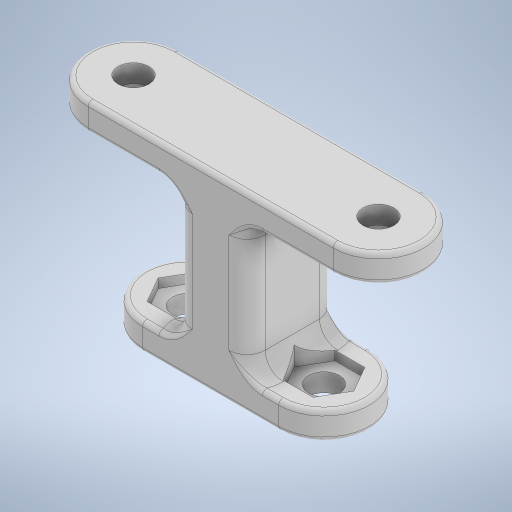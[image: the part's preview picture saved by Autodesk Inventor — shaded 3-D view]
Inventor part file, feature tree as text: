
AUTODESK INVENTOR PART (.ipt)
format: ipt  version: 2024.2 (Build 282272000, 272)  size: 423,936 bytes
history: native  units: mm
features: extrude x6, sketch x6, fillet x2
ambient origin geometry x8: Origin, YZ Plane, XZ Plane, XY Plane, X Axis, Y Axis, Z Axis, Center Point
bodies: Solid1 (feature_tree)
feature tree (14):
  extrude  "Extrusion1"  Depth=27.0mm
  extrude  "Extrusion2"  Depth=10.0mm TaperAngle=0.0deg
  extrude  "Extrusion3"  Depth=15.0mm
  extrude  "Extrusion4"  Depth=5.7mm
  extrude  "Extrusion5"  Depth=3.4mm
  extrude  "Extrusion6"  Depth=0.5mm
  fillet  "Fillet3"  Radius=1.0mm
  fillet  "Fillet2"  Radius=0.5mm
  sketch  "Sketch1"  dims[d0=3.4mm d1=27.0mm]
  sketch  "Sketch2"  dims[d2=10.0mm d3=3.0mm d4=0.0mm]
  sketch  "Sketch3"  dims[d5=15.0mm d6=0.0mm d7=15.0mm]
  sketch  "Sketch4"  dims[d8=3.0mm d9=0.0mm d10=5.7mm]
  sketch  "Sketch5"  dims[d11=1.0mm d12=0.0mm d13=3.4mm]
  sketch  "Sketch6"  dims[d14=2.0mm d15=0.0mm d16=5.1mm d17=1.0mm d18=0.0mm d20=0.5mm d22=8.0mm d23=2.0mm]
